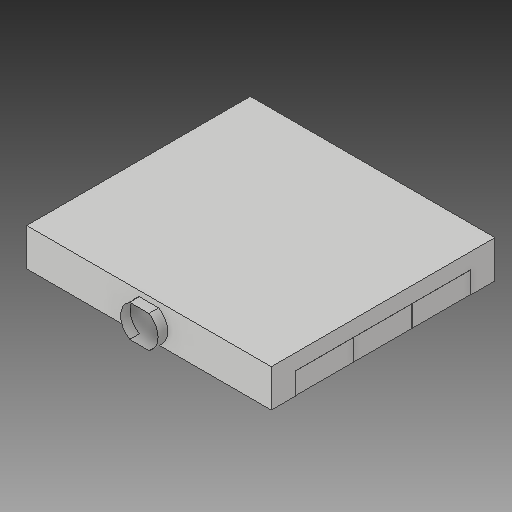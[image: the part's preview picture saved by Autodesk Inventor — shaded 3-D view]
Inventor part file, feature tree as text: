
AUTODESK INVENTOR PART (.ipt)
format: ipt  version: 2017 (Build 210142000, 142)  size: 294,912 bytes
history: native  units: in
note: dims shown in document units (in); Inventor stores cm internally (conversion verified against a paired STEP export)
features: extrude x6, sketch x4, delete_face x1
ambient origin geometry x8: Origin, YZ Plane, XZ Plane, XY Plane, X Axis, Y Axis, Z Axis, Center Point
bodies: Solid1 (feature_tree)
feature tree (11):
  extrude  "cubicals"  Depth=12.0in
  extrude  "floor"  Depth=2.5in
  extrude  "walls"  Depth=0.0833in
  extrude  "connection"  Depth=0.0833in
  extrude  "connection cut"  Depth=2.5in
  extrude  "ceiling"  Depth=2.5in
  delete_face  "Delete Face1"
  sketch  "Sketch2"  dims[d2=4.5in d3=0.0in d4=12.0in]
  sketch  "Sketch3"  dims[d5=8.0in d7=2.5in]
  sketch  "Sketch6"  dims[d10=0.0833in d95=0.0833in]
  sketch  "Sketch7"  dims[d97=0.0833in d98=0.0833in d99=12.0in d100=8.0in d102=0.0833in d103=0.0833in d104=0.0833in d105=0.0833in d106=12.0in d107=8.0in d109=0.0833in d110=0.0833in d111=0.0833in d112=0.0833in d113=2.5in d114=2.5in d115=3.0in d117=3.0in d118=6.0in d120=6.0in d121=1.0in d122=0.0in d128=1.0in d129=1.0in d130=1.0in d131=1.0in d132=1.0in d133=1.0in d134=7.7746in d135=0.0in d160=1.0in d161=0.0in d171=1.0in d172=0.0in d173=1.0in d174=0.0in d175=4.0in d177=3.8873in d178=3.8873in d182=1.6458in d187=3.3333in d188=1.0in d189=1.0in]
